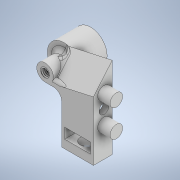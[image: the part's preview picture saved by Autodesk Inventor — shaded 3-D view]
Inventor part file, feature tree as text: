
AUTODESK INVENTOR PART (.ipt)
format: ipt  version: 2022.2 (Build 262287000, 287)  size: 1,422,336 bytes
history: native  units: mm
features: sketch x8, extrude x7, fillet x7, projected_geometry x5, other x4, draft x2, reference x2, plane x1, chamfer x1, hole x1, thread x1, revolve x1, helix x1
ambient origin geometry x8: Origin, YZ Plane, XZ Plane, XY Plane, X Axis, Y Axis, Z Axis, Center Point
bodies: Solid1 (feature_tree), Solid3 (feature_tree)
feature tree (41):
  extrude  "Extrusion1"  Depth=1.5mm TaperAngle=0.0deg
  fillet  "Fillet1"  Radius=2.0mm
  fillet  "Fillet2"  Radius=0.3mm
  sketch  "Sketch2"  dims[d0=2.2mm d10=1.5mm d11=0.0mm d15=2.0mm d16=0.3mm]
  extrude  "Extrusion4"  Depth=2.0mm TaperAngle=0.0deg
  extrude  "Extrusion5"  Depth=2.0mm TaperAngle=0.0deg
  draft  "FaceDraft4"
  fillet  "Fillet10"  Radius=3.0mm
  sketch  "Sketch8"  dims[d48=7.92mm d49=2.0mm d50=0.0mm d52=3.0mm]
  plane  "Work Plane1"
  extrude  "Extrusion6"  Depth=2.0mm
  extrude  "Extrusion7"  Depth=0.75mm
  chamfer  "Chamfer6"  Distance=1.99mm Angle=45.0deg
  draft  "FaceDraft5"
  fillet  "Fillet12"  Radius=1.116107mm
  fillet  "Fillet13"  Radius=9.599311mm
  extrude  "Extrusion8"  Depth=2.5mm
  fillet  "Fillet14"  Radius=0.7mm
  extrude  "Extrusion9"  Depth=7.0mm
  hole  "Hole1"  [1 undecoded]
  thread  "Thread2"  [1 undecoded]
  revolve  "Revolution2"  [1 undecoded]
  helix  "Coil2"  [1 undecoded]
  fillet  "Fillet15"  Radius=2.0mm
  projected_geometry  "Projected Loop2"
  projected_geometry  "Projected Loop3"
  sketch  "Sketch7"  dims[d23=3.0mm d24=0.0mm d44=2.0mm d45=0.0mm]
  projected_geometry  "Projected Loop4"
  sketch  "Sketch9"  dims[d53=3.0mm d54=0.0mm d57=2.0mm]
  reference  "Reference8"
  projected_geometry  "Projected Loop5"
  sketch  "Sketch13"  dims[d58=6.981317mm d59=0.75mm d61=1.99mm d62=1.0mm d63=45.0deg d66=1.116107mm d68=2.568591mm d76=9.599311mm]
  reference  "Reference9"
  sketch  "Sketch14"  dims[d88=6.2mm d89=2.5mm d90=0.7mm]
  projected_geometry  "Projected Loop6"
  sketch  "Sketch15"  dims[d91=0.7mm d92=7.0mm]
  sketch  "Sketch16"  dims[d94=2.0mm d95=3.0mm d96=5.0mm d97=0.5mm d98=-15.706218mm d99=2.0mm d103=1.0mm d104=0.0mm d105=0.0mm d106=1.0mm d107=3.2mm d108=9.5mm d109=0.0mm d110=2.18mm d111=6.0mm d112=6.0mm d113=4.0mm d114=90.0deg d115=8.0mm d116=20.594885mm d117=10.9mm d118=0.0mm d119=9.599311mm d120=0.064033mm d121=0.064033mm d124=0.4mm d126=9.599311mm d128=0.0mm d129=0.4004mm d130=11.7mm d131=10.0mm d132=0.0mm d133=0.0mm d134=0.0mm d135=0.0mm d136=0.0mm d137=1.0mm d36=0.5mm d37=0.872665mm d38=0.5mm d39=0.872665mm]
  other  "<userpath>\Documents\Inventor\Wire Bender\Assembly.iam"
  other  "Assembly.iam"
  other  "Crank:1"
  other  "Bending Base:1"
note: 4 required parameter values undecoded (feature->parameter linkage not recoverable at this tier; creation-order binding heuristic only, values carry confidence <= 0.55)